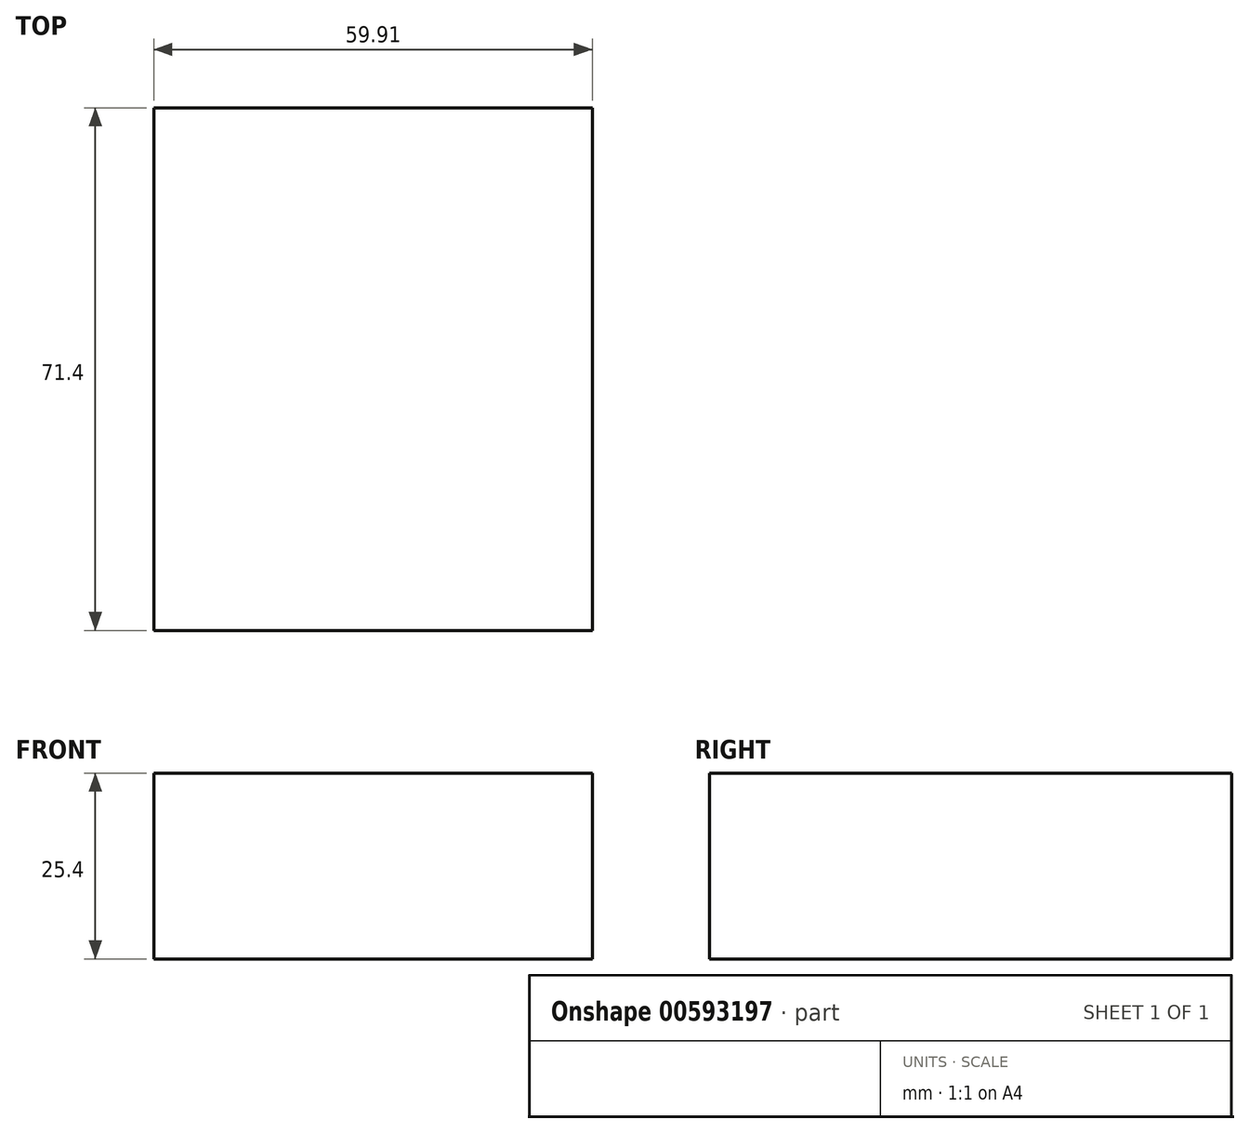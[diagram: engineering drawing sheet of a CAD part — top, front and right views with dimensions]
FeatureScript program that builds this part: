
annotation { "Feature Type Name" : "Feature", "Feature Type Description" : "" }
export const myFeature = defineFeature(function(context is Context, id is Id, definition is map)
    precondition{}
    {
        {
            var Q0;
            Q0=qCreatedBy(makeId("Top.planeOp"),FACE);
            var sketch = newSketch(context, id + "F0", { "sketchPlane" : qUnion([Q0])});
            skLineSegment(sketch, "E0.bottom", {"start": v(-21.61, 0) * mm, "end": v(-81.52, 0) * mm});
            skLineSegment(sketch, "E0.top", {"start": v(-21.61, -71.4) * mm, "end": v(-81.52, -71.4) * mm});
            skLineSegment(sketch, "E0.left", {"start": v(-21.61, 0) * mm, "end": v(-21.61, -71.4) * mm});
            skLineSegment(sketch, "E0.right", {"start": v(-81.52, 0) * mm, "end": v(-81.52, -71.4) * mm});
            skPoint(sketch, "E0.middle", {"position": v(-51.57, -35.7) * mm});
            skSolve(sketch);
        }
        {
            var Q0;
            Q0 = qSketchRegion(id + "F0", true);
            var sketch = newSketch(context, id + "F1", { "sketchPlane" : qUnion([Q0])});
            skSolve(sketch);
        }
        {
            var Q0;
            Q0=makeQuery(id+"F1.imprint","IMPRINT",FACE,{"disambiguationData":[TD([[makeQuery(id+"F1.imprint","IMPRINT",EDGE,{"derivedFrom":makeQuery(id+"F0.imprint","IMPRINT",EDGE,{"derivedFrom":sQuery(id+"F0.wireOp",EDGE,"E0.bottom")})}),1.0]])]});
            var sketch = newSketch(context, id + "F2", { "sketchPlane" : qUnion([Q0])});
            skSolve(sketch);
        }
        {
            var Q0;
            Q0=makeQuery(id+"F2.imprint","IMPRINT",FACE,{"disambiguationData":[TD([[makeQuery(id+"F2.imprint","IMPRINT",EDGE,{"derivedFrom":makeQuery(id+"F1.imprint","IMPRINT",EDGE,{"derivedFrom":makeQuery(id+"F0.imprint","IMPRINT",EDGE,{"derivedFrom":sQuery(id+"F0.wireOp",EDGE,"E0.bottom")})})}),1.0]])]});
            extrude(context, id + "F3", {"entities" : qUnion([Q0]), "depth" : 25.4 * mm, "offsetDistance" : 25.4 * mm});
        }
    });
